# Revit family: Plum Fix_Basin_Argent_Evo 650 Asymmetric Bowl_ RH
name_source: partatom
category: Plumbing Fixtures
revit_build: Autodesk Revit 2016 (Build: 20190508_0715(x64)
units: mm (PartAtom-declared; Revit-internal decimal feet)

## family parameters
Always vertical = Yes
Cut with Voids When Loaded = Yes
OmniClass Number = 23.45.05.14.14
OmniClass Title = Sinks/Lavatories
Part Type = Normal
Room Calculation Point = No
Round Connector Dimension = Use Diameter
Shared = No
Work Plane-Based = No

## types (3) — shared parameters
Body Material = z_Argent_Ceramic White
CW Connection = No
Description = Evo 650 Asymmetric Basin RH Bowl
HW Connection = No
IfcExportAs = IfcSanitaryTerminal
IfcExportType = WASHHANDBASIN
Manufacturer = Argent
Manufacturer_Overall Depth = 425 mm
Manufacturer_Overall Height = 110 mm  [stored 0.360892 ft]
Manufacturer_Overall Width = 650 mm  [stored 2.13255 ft]
Manufacturer_URL__Product Specific = https://www.argentaust.com.au
ModifiedIssue_ANZRS = 20200407 $
URL = https://www.argentaust.com.au
Uniclass2015Code = Pr_40_20_96_18
Uniclass2015Title = Countertop washbasins
Uniclass2015Version = Products v1.17
Vent Connection = No
Waste Connection = Yes
zero-valued in all types: CWFU, Cost, HWFU, WFU

## per-type parameters (varying)
| type | 1 Tap Hole | Manufacturer_Spec Code | Model | NoTap Hole | Trap Cover | Type Comments |
| 1 Tap Hole (FC29MUL01) | Yes | FC29MUL01 | FC29MUL01 | No | No | 1 Tap Hole |
| No Tap Hole (FC29MUL00) | No | FC29MUL00 | FC29MUL00 | Yes | No | No Tap Hole |
| 1 Tap Hole w. Trap Cover (FC29MUL01TB) | Yes | FC29MUL01TB | FC29MUL01TB | No | Yes | 1 Tap Hole w. Trap Cover |

note: [stored X ft] marks values corroborated as IEEE doubles in the binary element streams (Revit-internal decimal feet)

## geometry (parser evidence)
native form markers: Sweep x5
no freeform markers — native parametric forms only
